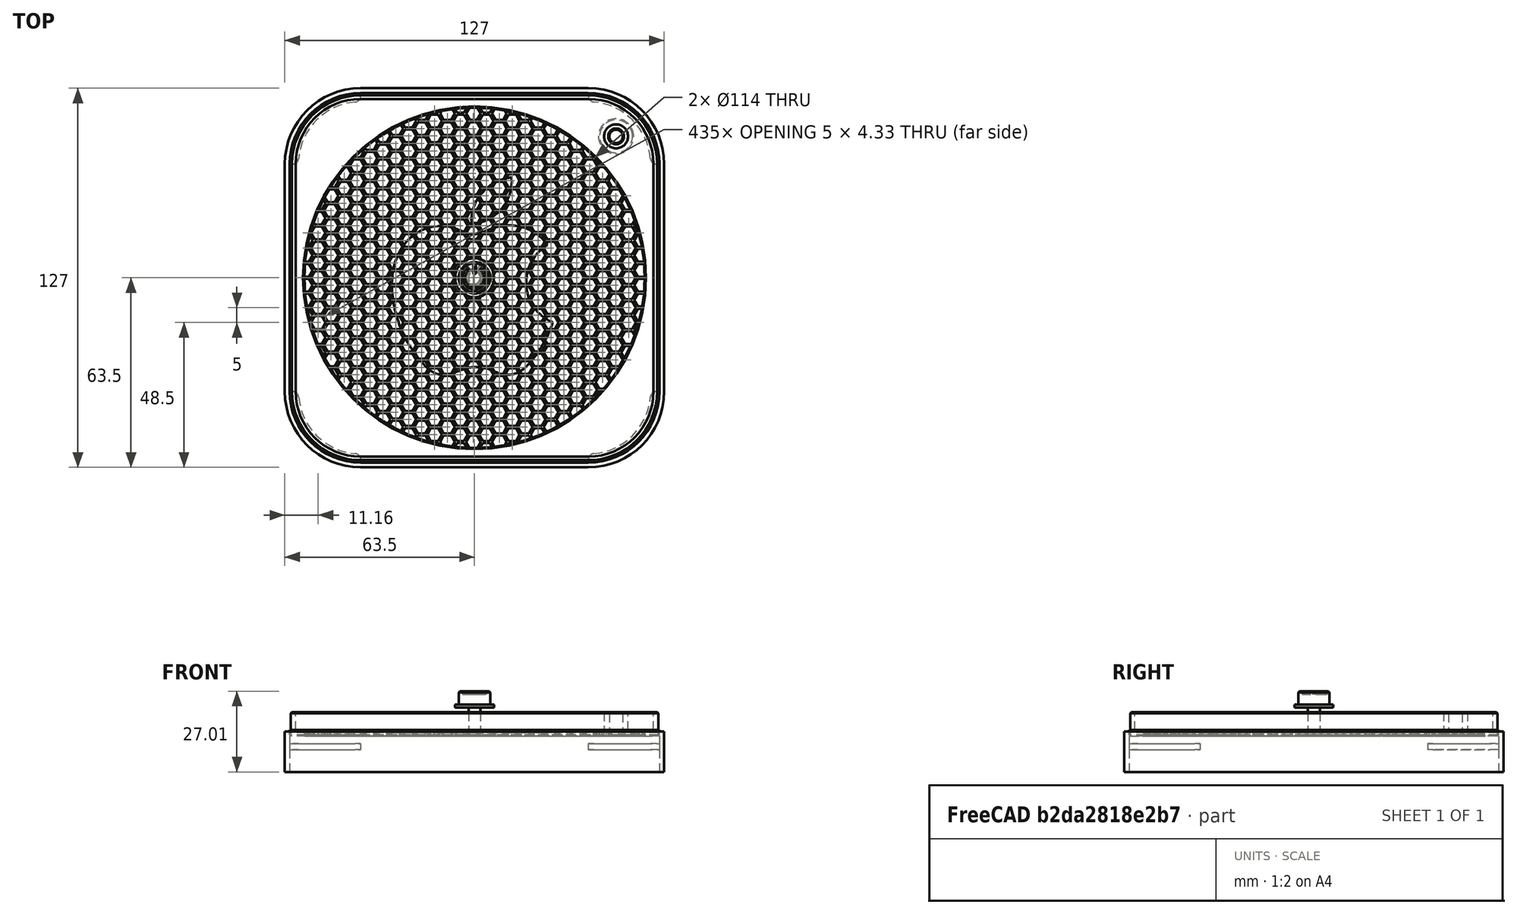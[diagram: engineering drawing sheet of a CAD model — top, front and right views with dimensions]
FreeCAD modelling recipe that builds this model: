
FCSTD DOCUMENT  (FreeCAD 1.0R39104 (Git))
Label: dust shroud for mac mini
License: All rights reserved
LicenseURL: http://en.wikipedia.org/wiki/All_rights_reserved
objects: Sketcher::SketchObject×13, PartDesign::Pad×8, PartDesign::Body×6, PartDesign::SubShapeBinder×4, PartDesign::Chamfer×3, Part::Extrusion×2, Part::Compound×2, App::FeaturePython×1, Part::FeaturePython×1, Part::Cylinder×1, Part::Cut×1, PartDesign::PolarPattern×1, Part::MultiFuse×1, PartDesign::Revolution×1
note: 81 computed .brp shape members not serialized (recipe doc carries the construction recipe); baked Part::Feature solids carry a one-line shape summary decoded from their .brp

FEATURE [App::FeaturePython] dd  # WARN: FeaturePython — macro-defined, semantics opaque (R4)
  BaseFloor = 2
  BaseWallHeight = 8
  BoxRadius = 25.4
  BoxWidth = 127
  ButtonDiameter = 11
  ButtonDistance = 67
  DynamicData = Created with DynamicData (v2.68) workbench. | This is a simple container object built | for holding custom properties.
  FrictionFit = 0
  Fudge = 0.4
  HexSize = 5
  HexSpacing = 5
  HexThickness = 1.6
  MeshThickness = 0.5
  RetainerThickness = 2
  RiserAngle = 0
  RiserHeight = 0
  RiserOuter = 114
  RiserTop = 97
  TopHeight = 12
  TopThickness = 1.6
  Wall = 1.6
  expr: HexThickness = TopThickness
FEATURE [Sketcher::SketchObject] Sketch005  label="master"
  ArcFitTolerance = 1e-06
  FullyConstrained = true
  MakeInternals = false
  MapMode = 5
  expr: Constraints[1] = dd.RiserOuter
  expr: Constraints[41] = dd.Wall
  expr: Constraints[5] = dd.ButtonDistance
  expr: Constraints[6] = dd.ButtonDiameter
  expr: Constraints[79] = dd.Fudge
  expr: Constraints[80] = dd.Wall
  expr: Constraints[81] = dd.RiserTop
  expr: Constraints[83] = dd.BoxRadius
  expr: Constraints[84] = dd.BoxWidth
  sketch-geometry (36):
    g0: Circle CenterX=3.1e-15 CenterY=3.4e-15 CenterZ=0 NormalX=0 NormalY=0 NormalZ=1 AngleXU=0 Radius=57
    g1: Circle CenterX=47.3762 CenterY=47.3762 CenterZ=0 NormalX=0 NormalY=0 NormalZ=1 AngleXU=0 Radius=5.5
    g2: LineSegment [constr] StartX=47.3762 StartY=47.3762 StartZ=0 EndX=3.1e-15 EndY=3.4e-15 EndZ=0
    g3: LineSegment StartX=-63.5 StartY=38.1 StartZ=0 EndX=-63.5 EndY=-38.1 EndZ=0
    g4: LineSegment StartX=-38.1 StartY=-63.5 StartZ=0 EndX=38.1 EndY=-63.5 EndZ=0
    g5: LineSegment StartX=63.5 StartY=-38.1 StartZ=0 EndX=63.5 EndY=38.1 EndZ=0
    g6: LineSegment StartX=38.1 StartY=63.5 StartZ=0 EndX=-38.1 EndY=63.5 EndZ=0
    g7: ArcOfCircle CenterX=-38.1 CenterY=38.1 CenterZ=0 NormalX=0 NormalY=0 NormalZ=1 AngleXU=0 Radius=25.4 StartAngle=1.5708 EndAngle=3.14159
    g8: ArcOfCircle CenterX=-38.1 CenterY=-38.1 CenterZ=0 NormalX=0 NormalY=0 NormalZ=1 AngleXU=0 Radius=25.4 StartAngle=3.14159 EndAngle=4.71239
    g9: ArcOfCircle CenterX=38.1 CenterY=-38.1 CenterZ=0 NormalX=0 NormalY=0 NormalZ=1 AngleXU=0 Radius=25.4 StartAngle=4.71239 EndAngle=6.28319
    g10: ArcOfCircle CenterX=38.1 CenterY=38.1 CenterZ=0 NormalX=0 NormalY=0 NormalZ=1 AngleXU=0 Radius=25.4 StartAngle=0 EndAngle=1.5708
    g11: LineSegment StartX=-61.9 StartY=38.1 StartZ=0 EndX=-61.9 EndY=-38.1 EndZ=0
    g12: LineSegment StartX=-38.1 StartY=-61.9 StartZ=0 EndX=38.1 EndY=-61.9 EndZ=0
    g13: LineSegment StartX=61.9 StartY=-38.1 StartZ=0 EndX=61.9 EndY=38.1 EndZ=0
    g14: LineSegment StartX=38.1 StartY=61.9 StartZ=0 EndX=-38.1 EndY=61.9 EndZ=0
    g15: ArcOfCircle CenterX=-38.1 CenterY=38.1 CenterZ=0 NormalX=0 NormalY=0 NormalZ=1 AngleXU=0 Radius=23.8 StartAngle=1.5708 EndAngle=3.14159
    g16: ArcOfCircle CenterX=-38.1 CenterY=-38.1 CenterZ=0 NormalX=0 NormalY=0 NormalZ=1 AngleXU=0 Radius=23.8 StartAngle=3.14159 EndAngle=4.71239
    g17: ArcOfCircle CenterX=38.1 CenterY=-38.1 CenterZ=0 NormalX=0 NormalY=0 NormalZ=1 AngleXU=0 Radius=23.8 StartAngle=4.71239 EndAngle=6.28319
    g18: ArcOfCircle CenterX=38.1 CenterY=38.1 CenterZ=0 NormalX=0 NormalY=0 NormalZ=1 AngleXU=0 Radius=23.8 StartAngle=-2.6086e-12 EndAngle=1.5708
    g19: Circle CenterX=3.1e-15 CenterY=3.4e-15 CenterZ=0 NormalX=0 NormalY=0 NormalZ=1 AngleXU=0 Radius=48.5
    g20: LineSegment StartX=-61.5 StartY=38.1 StartZ=0 EndX=-61.5 EndY=-38.1 EndZ=0
    g21: LineSegment StartX=-38.1 StartY=-61.5 StartZ=0 EndX=38.1 EndY=-61.5 EndZ=0
    g22: LineSegment StartX=61.5 StartY=-38.1 StartZ=0 EndX=61.5 EndY=38.1 EndZ=0
    g23: LineSegment StartX=38.1 StartY=61.5 StartZ=0 EndX=-38.1 EndY=61.5 EndZ=0
    g24: ArcOfCircle CenterX=-38.1 CenterY=38.1 CenterZ=0 NormalX=0 NormalY=0 NormalZ=1 AngleXU=0 Radius=23.4 StartAngle=1.5708 EndAngle=3.14159
    g25: ArcOfCircle CenterX=-38.1 CenterY=-38.1 CenterZ=0 NormalX=0 NormalY=0 NormalZ=1 AngleXU=0 Radius=23.4 StartAngle=3.14159 EndAngle=4.71239
    g26: ArcOfCircle CenterX=38.1 CenterY=-38.1 CenterZ=0 NormalX=0 NormalY=0 NormalZ=1 AngleXU=0 Radius=23.4 StartAngle=4.71239 EndAngle=6.28319
    g27: ArcOfCircle CenterX=38.1 CenterY=38.1 CenterZ=0 NormalX=0 NormalY=0 NormalZ=1 AngleXU=0 Radius=23.4 StartAngle=-3.471e-12 EndAngle=1.5708
    g28: LineSegment StartX=-59.9 StartY=38.1 StartZ=0 EndX=-59.9 EndY=-38.1 EndZ=0
    g29: LineSegment StartX=-38.1 StartY=-59.9 StartZ=0 EndX=38.1 EndY=-59.9 EndZ=0
    g30: LineSegment StartX=59.9 StartY=-38.1 StartZ=0 EndX=59.9 EndY=38.1 EndZ=0
    g31: LineSegment StartX=38.1 StartY=59.9 StartZ=0 EndX=-38.1 EndY=59.9 EndZ=0
    g32: ArcOfCircle CenterX=-38.1 CenterY=38.1 CenterZ=0 NormalX=0 NormalY=0 NormalZ=1 AngleXU=0 Radius=21.8 StartAngle=1.5708 EndAngle=3.14159
    g33: ArcOfCircle CenterX=-38.1 CenterY=-38.1 CenterZ=0 NormalX=0 NormalY=0 NormalZ=1 AngleXU=0 Radius=21.8 StartAngle=3.14159 EndAngle=4.71239
    g34: ArcOfCircle CenterX=38.1 CenterY=-38.1 CenterZ=0 NormalX=0 NormalY=0 NormalZ=1 AngleXU=0 Radius=21.8 StartAngle=4.71239 EndAngle=6.28319
    g35: ArcOfCircle CenterX=38.1 CenterY=38.1 CenterZ=0 NormalX=0 NormalY=0 NormalZ=1 AngleXU=0 Radius=21.8 StartAngle=-1.30367e-11 EndAngle=1.5708
  constraints (85):
    c: Coincident(g0,g-1)
    c: Diameter(g0) = 114
    c: Coincident(g2,g1)
    c: Coincident(g2,g0)
    c: Angle(g-1,g2) = 0.785398
    c: Distance(g2) = 67
    c: Diameter(g1) = 11
    c: Tangent(g3,g7) = -1.5708
    c: Tangent(g3,g8) = -1.5708
    c: Tangent(g4,g8) = -1.5708
    c: Tangent(g4,g9) = -1.5708
    c: Tangent(g5,g9) = -1.5708
    c: Tangent(g5,g10) = -1.5708
    c: Tangent(g6,g10) = -1.5708
    c: Tangent(g6,g7) = -1.5708
    c: Vertical(g3)
    c: Vertical(g5)
    c: Horizontal(g4)
    c: Horizontal(g6)
    c: Equal(g7,g8)
    c: Equal(g8,g9)
    c: Equal(g9,g10)
    c: Symmetric(g8,g10,g0)
    c: Equal(g6,g3)
    c: Tangent(g11,g15) = -1.5708
    c: Tangent(g11,g16) = -1.5708
    c: Tangent(g12,g16) = -1.5708
    c: Tangent(g12,g17) = -1.5708
    c: Tangent(g13,g17) = -1.5708
    c: Tangent(g13,g18) = -1.5708
    c: Tangent(g14,g18) = -1.5708
    c: Tangent(g14,g15) = -1.5708
    c: Vertical(g11)
    c: Vertical(g13)
    c: Horizontal(g12)
    c: Horizontal(g14)
    c: Equal(g15,g16)
    c: Equal(g16,g17)
    c: Equal(g17,g18)
    c: Symmetric(g16,g18,g0)
    c: Equal(g14,g11)
    c: DistanceY(g14,g6) = 1.6
    c: Coincident(g19,g0)
    c: Tangent(g20,g24) = -1.5708
    c: Tangent(g20,g25) = -1.5708
    c: Tangent(g21,g25) = -1.5708
    c: Tangent(g21,g26) = -1.5708
    c: Tangent(g22,g26) = -1.5708
    c: Tangent(g22,g27) = -1.5708
    c: Tangent(g23,g27) = -1.5708
    c: Tangent(g23,g24) = -1.5708
    c: Vertical(g20)
    c: Vertical(g22)
    c: Horizontal(g21)
    c: Horizontal(g23)
    c: Equal(g24,g25)
    c: Equal(g25,g26)
    c: Equal(g26,g27)
    c: Symmetric(g27,g25,g0)
    c: Equal(g23,g20)
    c: Vertical(g23,g14)
    c: Tangent(g28,g32) = -1.5708
    c: Tangent(g28,g33) = -1.5708
    c: Tangent(g29,g33) = -1.5708
    c: Tangent(g29,g34) = -1.5708
    c: Tangent(g30,g34) = -1.5708
    c: Tangent(g30,g35) = -1.5708
    c: Tangent(g31,g35) = -1.5708
    c: Tangent(g31,g32) = -1.5708
    c: Vertical(g28)
    c: Vertical(g30)
    c: Horizontal(g29)
    c: Horizontal(g31)
    c: Equal(g32,g33)
    c: Equal(g33,g34)
    c: Equal(g34,g35)
    c: Symmetric(g33,g35,g0)
    c: Equal(g30,g31)
    c: Vertical(g31,g23)
    c: DistanceY(g23,g14) = 0.4
    c: DistanceY(g31,g23) = 1.6
    c: Diameter(g19) = 97
    c: Vertical(g14,g6)
    c: Radius(g7) = 25.4
    c: DistanceX(g3,g5) = 127
FEATURE [PartDesign::SubShapeBinder] Binder
  BindCopyOnChange = 0
  BindMode = 0
  ClaimChildren = false
  Context = -> Body003 [Binder.]
  Fuse = false
  MakeFace = true
  OffsetFill = false
  OffsetIntersection = false
  OffsetJoinType = 0
  OffsetOpenResult = false
  PartialLoad = false
  Refine = true
  Relative = true
  Support = -> [Sketch005]
  _Version = 2
FEATURE [Sketcher::SketchObject] Sketch006
  ArcFitTolerance = 1e-06
  AttachmentSupport = -> [XY_Plane003]
  ExternalGeometry = -> [Binder]
  FullyConstrained = true
  MakeInternals = false
  MapMode = 5
  sketch-geometry (12):
    g0: Circle CenterX=0 CenterY=0 CenterZ=0 NormalX=0 NormalY=0 NormalZ=1 AngleXU=0 Radius=57
    g1: Circle CenterX=47.3762 CenterY=47.3762 CenterZ=0 NormalX=0 NormalY=0 NormalZ=1 AngleXU=0 Radius=5.5
    g2: LineSegment StartX=-63.5 StartY=38.1 StartZ=0 EndX=-63.5 EndY=-38.1 EndZ=0
    g3: LineSegment StartX=-38.1 StartY=-63.5 StartZ=0 EndX=38.1 EndY=-63.5 EndZ=0
    g4: LineSegment StartX=63.5 StartY=-38.1 StartZ=0 EndX=63.5 EndY=38.1 EndZ=0
    g5: LineSegment StartX=38.1 StartY=63.5 StartZ=0 EndX=-38.1 EndY=63.5 EndZ=0
    g6: ArcOfCircle CenterX=-38.1 CenterY=38.1 CenterZ=0 NormalX=0 NormalY=0 NormalZ=1 AngleXU=0 Radius=25.4 StartAngle=1.5708 EndAngle=3.14159
    g7: ArcOfCircle CenterX=-38.1 CenterY=-38.1 CenterZ=0 NormalX=0 NormalY=0 NormalZ=1 AngleXU=0 Radius=25.4 StartAngle=3.14159 EndAngle=4.71239
    g8: ArcOfCircle CenterX=38.1 CenterY=-38.1 CenterZ=0 NormalX=0 NormalY=0 NormalZ=1 AngleXU=0 Radius=25.4 StartAngle=4.71239 EndAngle=6.28319
    g9: ArcOfCircle CenterX=38.1 CenterY=38.1 CenterZ=0 NormalX=0 NormalY=0 NormalZ=1 AngleXU=0 Radius=25.4 StartAngle=0 EndAngle=1.5708
    g10: GeomPoint [constr] X=-63.5 Y=63.5 Z=0
    g11: GeomPoint [constr] X=63.5 Y=-63.5 Z=0
  constraints (26):
    c: Coincident(g0,g-1)
    c: Coincident(g1,g-5)
    c: Equal(g1,g-5)
    c: Equal(g0,g-4)
    c: Tangent(g2,g6) = -1.5708
    c: Tangent(g2,g7) = -1.5708
    c: Tangent(g3,g7) = -1.5708
    c: Tangent(g3,g8) = -1.5708
    c: Tangent(g4,g8) = -1.5708
    c: Tangent(g4,g9) = -1.5708
    c: Tangent(g5,g9) = -1.5708
    c: Tangent(g5,g6) = -1.5708
    c: Vertical(g2)
    c: Vertical(g4)
    c: Horizontal(g3)
    c: Horizontal(g5)
    c: Equal(g6,g7)
    c: Equal(g7,g8)
    c: Equal(g8,g9)
    c: PointOnObject(g10,g2)
    c: PointOnObject(g10,g5)
    c: PointOnObject(g11,g3)
    c: PointOnObject(g11,g4)
    c: Equal(g5,g2)
    c: Symmetric(g6,g8,g0)
    c: Coincident(g5,g-3)
FEATURE [PartDesign::Pad] Pad004
  Direction = (0,0,1)
  Length = 1.6
  Length2 = 10
  Profile = -> Sketch006
  ReferenceAxis = -> Sketch006 [N_Axis]
  Refine = true
  Suppressed = false
  Type = 0
  expr: Length = dd.TopThickness
FEATURE [Sketcher::SketchObject] Sketch007
  ArcFitTolerance = 1e-06
  AttachmentSupport = -> [XY_Plane003]
  ExternalGeometry = -> [Binder]
  FullyConstrained = true
  MakeInternals = false
  MapMode = 5
  sketch-geometry (20):
    g0: LineSegment StartX=-61.9 StartY=38.1 StartZ=0 EndX=-61.9 EndY=-38.1 EndZ=0
    g1: LineSegment StartX=-38.1 StartY=-61.9 StartZ=0 EndX=38.1 EndY=-61.9 EndZ=0
    g2: LineSegment StartX=61.9 StartY=-38.1 StartZ=0 EndX=61.9 EndY=38.1 EndZ=0
    g3: LineSegment StartX=38.1 StartY=61.9 StartZ=0 EndX=-38.1 EndY=61.9 EndZ=0
    g4: ArcOfCircle CenterX=-38.1 CenterY=38.1 CenterZ=0 NormalX=0 NormalY=0 NormalZ=1 AngleXU=0 Radius=23.8 StartAngle=1.5708 EndAngle=3.14159
    g5: ArcOfCircle CenterX=-38.1 CenterY=-38.1 CenterZ=0 NormalX=0 NormalY=0 NormalZ=1 AngleXU=0 Radius=23.8 StartAngle=3.14159 EndAngle=4.71239
    g6: ArcOfCircle CenterX=38.1 CenterY=-38.1 CenterZ=0 NormalX=0 NormalY=0 NormalZ=1 AngleXU=0 Radius=23.8 StartAngle=4.71239 EndAngle=6.28319
    g7: ArcOfCircle CenterX=38.1 CenterY=38.1 CenterZ=0 NormalX=0 NormalY=0 NormalZ=1 AngleXU=0 Radius=23.8 StartAngle=0 EndAngle=1.5708
    g8: GeomPoint [constr] X=-61.9 Y=61.9 Z=0
    g9: GeomPoint [constr] X=61.9 Y=-61.9 Z=0
    g10: LineSegment StartX=-63.5 StartY=38.1 StartZ=0 EndX=-63.5 EndY=-38.1 EndZ=0
    g11: LineSegment StartX=-38.1 StartY=-63.5 StartZ=0 EndX=38.1 EndY=-63.5 EndZ=0
    g12: LineSegment StartX=63.5 StartY=-38.1 StartZ=0 EndX=63.5 EndY=38.1 EndZ=0
    g13: LineSegment StartX=38.1 StartY=63.5 StartZ=0 EndX=-38.1 EndY=63.5 EndZ=0
    g14: ArcOfCircle CenterX=-38.1 CenterY=38.1 CenterZ=0 NormalX=0 NormalY=0 NormalZ=1 AngleXU=0 Radius=25.4 StartAngle=1.5708 EndAngle=3.14159
    g15: ArcOfCircle CenterX=-38.1 CenterY=-38.1 CenterZ=0 NormalX=0 NormalY=0 NormalZ=1 AngleXU=0 Radius=25.4 StartAngle=3.14159 EndAngle=4.71239
    g16: ArcOfCircle CenterX=38.1 CenterY=-38.1 CenterZ=0 NormalX=0 NormalY=0 NormalZ=1 AngleXU=0 Radius=25.4 StartAngle=4.71239 EndAngle=6.28319
    g17: ArcOfCircle CenterX=38.1 CenterY=38.1 CenterZ=0 NormalX=0 NormalY=0 NormalZ=1 AngleXU=0 Radius=25.4 StartAngle=0 EndAngle=1.5708
    g18: GeomPoint [constr] X=-63.5 Y=63.5 Z=0
    g19: GeomPoint [constr] X=63.5 Y=-63.5 Z=0
  constraints (44):
    c: Tangent(g0,g4) = -1.5708
    c: Tangent(g0,g5) = -1.5708
    c: Tangent(g1,g5) = -1.5708
    c: Tangent(g1,g6) = -1.5708
    c: Tangent(g2,g6) = -1.5708
    c: Tangent(g2,g7) = -1.5708
    c: Tangent(g3,g7) = -1.5708
    c: Tangent(g3,g4) = -1.5708
    c: Vertical(g0)
    c: Vertical(g2)
    c: Horizontal(g1)
    c: Horizontal(g3)
    c: Equal(g4,g5)
    c: Equal(g5,g6)
    c: Equal(g6,g7)
    c: PointOnObject(g8,g0)
    c: PointOnObject(g8,g3)
    c: PointOnObject(g9,g1)
    c: PointOnObject(g9,g2)
    c: Tangent(g10,g14) = -1.5708
    c: Tangent(g10,g15) = -1.5708
    c: Tangent(g11,g15) = -1.5708
    c: Tangent(g11,g16) = -1.5708
    c: Tangent(g12,g16) = -1.5708
    c: Tangent(g12,g17) = -1.5708
    c: Tangent(g13,g17) = -1.5708
    c: Tangent(g13,g14) = -1.5708
    c: Vertical(g10)
    c: Vertical(g12)
    c: Horizontal(g11)
    c: Horizontal(g13)
    c: Equal(g14,g15)
    c: Equal(g15,g16)
    c: Equal(g16,g17)
    c: PointOnObject(g18,g10)
    c: PointOnObject(g18,g13)
    c: PointOnObject(g19,g11)
    c: PointOnObject(g19,g12)
    c: Equal(g10,g13)
    c: Symmetric(g14,g16,g-1)
    c: Symmetric(g9,g8,g-1)
    c: Coincident(g13,g-3)
    c: Coincident(g3,g-4)
    c: Equal(g0,g3)
FEATURE [PartDesign::Pad] Pad005
  BaseFeature = -> Pad004
  Direction = (0,0,1)
  Length = 12
  Length2 = 10
  Profile = -> Sketch007
  ReferenceAxis = -> Sketch007 [N_Axis]
  Refine = true
  Reversed = true
  Suppressed = false
  Type = 0
  expr: Length = dd.TopHeight
FEATURE [PartDesign::SubShapeBinder] Binder001
  BindCopyOnChange = 0
  BindMode = 0
  ClaimChildren = false
  Context = -> Body [Binder001.]
  Fuse = false
  MakeFace = true
  OffsetFill = false
  OffsetIntersection = false
  OffsetJoinType = 0
  OffsetOpenResult = false
  PartialLoad = false
  Refine = true
  Relative = true
  Support = -> [Sketch005]
  _Version = 2
FEATURE [Sketcher::SketchObject] Sketch
  ArcFitTolerance = 1e-06
  AttachmentSupport = -> [XY_Plane]
  ExternalGeometry = -> [Binder001]
  FullyConstrained = true
  MakeInternals = false
  MapMode = 5
  expr: Constraints[25] = dd.FrictionFit
  sketch-geometry (12):
    g0: Circle CenterX=47.3762 CenterY=47.3762 CenterZ=0 NormalX=0 NormalY=0 NormalZ=1 AngleXU=0 Radius=2.25
    g1: Circle CenterX=0 CenterY=0 CenterZ=0 NormalX=0 NormalY=0 NormalZ=1 AngleXU=0 Radius=57
    g2: LineSegment StartX=-61.9 StartY=38.1 StartZ=0 EndX=-61.9 EndY=-38.1 EndZ=0
    g3: LineSegment StartX=-38.1 StartY=-61.9 StartZ=0 EndX=38.1 EndY=-61.9 EndZ=0
    g4: LineSegment StartX=61.9 StartY=-38.1 StartZ=0 EndX=61.9 EndY=38.1 EndZ=0
    g5: LineSegment StartX=38.1 StartY=61.9 StartZ=0 EndX=-38.1 EndY=61.9 EndZ=0
    g6: ArcOfCircle CenterX=-38.1 CenterY=38.1 CenterZ=0 NormalX=0 NormalY=0 NormalZ=1 AngleXU=0 Radius=23.8 StartAngle=1.5708 EndAngle=3.14159
    g7: ArcOfCircle CenterX=-38.1 CenterY=-38.1 CenterZ=0 NormalX=0 NormalY=0 NormalZ=1 AngleXU=0 Radius=23.8 StartAngle=3.14159 EndAngle=4.71239
    g8: ArcOfCircle CenterX=38.1 CenterY=-38.1 CenterZ=0 NormalX=0 NormalY=0 NormalZ=1 AngleXU=0 Radius=23.8 StartAngle=4.71239 EndAngle=6.28319
    g9: ArcOfCircle CenterX=38.1 CenterY=38.1 CenterZ=0 NormalX=0 NormalY=0 NormalZ=1 AngleXU=0 Radius=23.8 StartAngle=0 EndAngle=1.5708
    g10: GeomPoint [constr] X=-61.9 Y=61.9 Z=0
    g11: GeomPoint [constr] X=61.9 Y=-61.9 Z=0
  constraints (27):
    c: Coincident(g0,g-3)
    c: Coincident(g1,g-1)
    c: Equal(g1,g-4)
    c: Tangent(g2,g6) = -1.5708
    c: Tangent(g2,g7) = -1.5708
    c: Tangent(g3,g7) = -1.5708
    c: Tangent(g3,g8) = -1.5708
    c: Tangent(g4,g8) = -1.5708
    c: Tangent(g4,g9) = -1.5708
    c: Tangent(g5,g9) = -1.5708
    c: Tangent(g5,g6) = -1.5708
    c: Vertical(g2)
    c: Vertical(g4)
    c: Horizontal(g3)
    c: Horizontal(g5)
    c: Equal(g6,g7)
    c: Equal(g7,g8)
    c: Equal(g8,g9)
    c: PointOnObject(g10,g2)
    c: PointOnObject(g10,g5)
    c: PointOnObject(g11,g3)
    c: PointOnObject(g11,g4)
    c: Symmetric(g7,g9,g1)
    c: Equal(g5,g2)
    c: Vertical(g5,g-5)
    c: DistanceY(g5,g-5) = 0
    c: Diameter(g0) = 4.5
FEATURE [PartDesign::Pad] Pad
  Direction = (0,0,1)
  Length = 2
  Length2 = 10
  Profile = -> Sketch
  ReferenceAxis = -> Sketch [N_Axis]
  Refine = true
  Suppressed = false
  Type = 0
  expr: Length = dd.BaseFloor
FEATURE [Sketcher::SketchObject] Sketch008
  ArcFitTolerance = 1e-06
  AttachmentSupport = -> [XY_Plane]
  ExternalGeometry = -> [Binder001]
  FullyConstrained = true
  MakeInternals = false
  MapMode = 5
  sketch-geometry (20):
    g0: LineSegment StartX=-59.9 StartY=38.1 StartZ=0 EndX=-59.9 EndY=-38.1 EndZ=0
    g1: LineSegment StartX=-38.1 StartY=-59.9 StartZ=0 EndX=38.1 EndY=-59.9 EndZ=0
    g2: LineSegment StartX=59.9 StartY=-38.1 StartZ=0 EndX=59.9 EndY=38.1 EndZ=0
    g3: LineSegment StartX=38.1 StartY=59.9 StartZ=0 EndX=-38.1 EndY=59.9 EndZ=0
    g4: ArcOfCircle CenterX=-38.1 CenterY=38.1 CenterZ=0 NormalX=0 NormalY=0 NormalZ=1 AngleXU=0 Radius=21.8 StartAngle=1.5708 EndAngle=3.14159
    g5: ArcOfCircle CenterX=-38.1 CenterY=-38.1 CenterZ=0 NormalX=0 NormalY=0 NormalZ=1 AngleXU=0 Radius=21.8 StartAngle=3.14159 EndAngle=4.71239
    g6: ArcOfCircle CenterX=38.1 CenterY=-38.1 CenterZ=0 NormalX=0 NormalY=0 NormalZ=1 AngleXU=0 Radius=21.8 StartAngle=4.71239 EndAngle=6.28319
    g7: ArcOfCircle CenterX=38.1 CenterY=38.1 CenterZ=0 NormalX=0 NormalY=0 NormalZ=1 AngleXU=0 Radius=21.8 StartAngle=1e-16 EndAngle=1.5708
    g8: GeomPoint [constr] X=-59.9 Y=59.9 Z=0
    g9: GeomPoint [constr] X=59.9 Y=-59.9 Z=0
    g10: LineSegment StartX=-61.5 StartY=38.1 StartZ=0 EndX=-61.5 EndY=-38.1 EndZ=0
    g11: LineSegment StartX=-38.1 StartY=-61.5 StartZ=0 EndX=38.1 EndY=-61.5 EndZ=0
    g12: LineSegment StartX=61.5 StartY=-38.1 StartZ=0 EndX=61.5 EndY=38.1 EndZ=0
    g13: LineSegment StartX=38.1 StartY=61.5 StartZ=0 EndX=-38.1 EndY=61.5 EndZ=0
    g14: ArcOfCircle CenterX=-38.1 CenterY=38.1 CenterZ=0 NormalX=0 NormalY=0 NormalZ=1 AngleXU=0 Radius=23.4 StartAngle=1.5708 EndAngle=3.14159
    g15: ArcOfCircle CenterX=-38.1 CenterY=-38.1 CenterZ=0 NormalX=0 NormalY=0 NormalZ=1 AngleXU=0 Radius=23.4 StartAngle=3.14159 EndAngle=4.71239
    g16: ArcOfCircle CenterX=38.1 CenterY=-38.1 CenterZ=0 NormalX=0 NormalY=0 NormalZ=1 AngleXU=0 Radius=23.4 StartAngle=4.71239 EndAngle=6.28319
    g17: ArcOfCircle CenterX=38.1 CenterY=38.1 CenterZ=0 NormalX=0 NormalY=0 NormalZ=1 AngleXU=0 Radius=23.4 StartAngle=1e-16 EndAngle=1.5708
    g18: GeomPoint [constr] X=-61.5 Y=61.5 Z=0
    g19: GeomPoint [constr] X=61.5 Y=-61.5 Z=0
  constraints (44):
    c: Tangent(g0,g4) = -1.5708
    c: Tangent(g0,g5) = -1.5708
    c: Tangent(g1,g5) = -1.5708
    c: Tangent(g1,g6) = -1.5708
    c: Tangent(g2,g6) = -1.5708
    c: Tangent(g2,g7) = -1.5708
    c: Tangent(g3,g7) = -1.5708
    c: Tangent(g3,g4) = -1.5708
    c: Vertical(g0)
    c: Vertical(g2)
    c: Horizontal(g1)
    c: Horizontal(g3)
    c: Equal(g4,g5)
    c: Equal(g5,g6)
    c: Equal(g6,g7)
    c: PointOnObject(g8,g0)
    c: PointOnObject(g8,g3)
    c: PointOnObject(g9,g1)
    c: PointOnObject(g9,g2)
    c: Tangent(g10,g14) = -1.5708
    c: Tangent(g10,g15) = -1.5708
    c: Tangent(g11,g15) = -1.5708
    c: Tangent(g11,g16) = -1.5708
    c: Tangent(g12,g16) = -1.5708
    c: Tangent(g12,g17) = -1.5708
    c: Tangent(g13,g17) = -1.5708
    c: Tangent(g13,g14) = -1.5708
    c: Vertical(g10)
    c: Vertical(g12)
    c: Horizontal(g11)
    c: Horizontal(g13)
    c: Equal(g14,g15)
    c: Equal(g15,g16)
    c: Equal(g16,g17)
    c: PointOnObject(g18,g10)
    c: PointOnObject(g18,g13)
    c: PointOnObject(g19,g11)
    c: PointOnObject(g19,g12)
    c: Equal(g10,g13)
    c: Equal(g3,g0)
    c: Symmetric(g4,g6,g-1)
    c: Symmetric(g14,g16,g-1)
    c: Coincident(g13,g-4)
    c: Coincident(g3,g-3)
FEATURE [PartDesign::Pad] Pad006
  BaseFeature = -> Pad
  Direction = (0,0,1)
  Length = 8
  Length2 = 10
  Profile = -> Sketch008
  ReferenceAxis = -> Sketch008 [N_Axis]
  Refine = true
  Suppressed = false
  Type = 0
  expr: Length = dd.BaseWallHeight
FEATURE [Sketcher::SketchObject] Sketch011
  ArcFitTolerance = 1e-06
  FullyConstrained = true
  MakeInternals = false
  expr: Constraints[39] = dd.HexSpacing
  expr: Constraints[40] = dd.HexSize
  sketch-geometry (15):
    g0: LineSegment StartX=1.25 StartY=-2.16506 StartZ=0 EndX=2.5 EndY=8e-16 EndZ=0
    g1: LineSegment StartX=2.5 StartY=8e-16 StartZ=0 EndX=1.25 EndY=2.16506 EndZ=0
    g2: LineSegment StartX=1.25 StartY=2.16506 StartZ=0 EndX=-1.25 EndY=2.16506 EndZ=0
    g3: LineSegment StartX=-1.25 StartY=2.16506 StartZ=0 EndX=-2.5 EndY=2.84e-14 EndZ=0
    g4: LineSegment StartX=-2.5 StartY=2.84e-14 StartZ=0 EndX=-1.25 EndY=-2.16506 EndZ=0
    g5: LineSegment StartX=-1.25 StartY=-2.16506 StartZ=0 EndX=1.25 EndY=-2.16506 EndZ=0
    g6: Circle [constr] CenterX=-2e-16 CenterY=0 CenterZ=0 NormalX=0 NormalY=0 NormalZ=1 AngleXU=0 Radius=2.5
    g7: LineSegment StartX=5.58013 StartY=-4.66506 StartZ=0 EndX=6.83013 EndY=-2.5 EndZ=0
    g8: LineSegment StartX=6.83013 StartY=-2.5 StartZ=0 EndX=5.58013 EndY=-0.334936 EndZ=0
    g9: LineSegment StartX=5.58013 StartY=-0.334936 StartZ=0 EndX=3.08013 EndY=-0.334936 EndZ=0
    g10: LineSegment StartX=3.08013 StartY=-0.334936 StartZ=0 EndX=1.83013 EndY=-2.5 EndZ=0
    g11: LineSegment StartX=1.83013 StartY=-2.5 StartZ=0 EndX=3.08013 EndY=-4.66506 EndZ=0
    g12: LineSegment StartX=3.08013 StartY=-4.66506 StartZ=0 EndX=5.58013 EndY=-4.66506 EndZ=0
    g13: Circle [constr] CenterX=4.33013 CenterY=-2.5 CenterZ=0 NormalX=0 NormalY=0 NormalZ=1 AngleXU=0 Radius=2.5
    g14: LineSegment [constr] StartX=4.33013 StartY=-2.5 StartZ=0 EndX=-2e-16 EndY=0 EndZ=0
  constraints (35):
    c: Coincident(g0,g1)
    c: Coincident(g1,g2)
    c: Coincident(g2,g3)
    c: Coincident(g3,g4)
    c: Coincident(g4,g5)
    c: Coincident(g5,g0)
    c: Equal(g0, g1-g5) x5
    c: PointOnObject(g0,g6)
    c: PointOnObject(g1,g6)
    c: PointOnObject(g2,g6)
    c: PointOnObject(g3,g6)
    c: PointOnObject(g4,g6)
    c: PointOnObject(g5,g6)
    c: Coincident(g7,g8)
    c: Coincident(g8,g9)
    c: Coincident(g9,g10)
    c: Coincident(g10,g11)
    c: Coincident(g11,g12)
    c: Coincident(g12,g7)
    c: Equal(g7, g8-g12) x5
    c: PointOnObject(g7,g13)
    c: PointOnObject(g8,g13)
    c: PointOnObject(g9,g13)
    c: PointOnObject(g10,g13)
    c: PointOnObject(g11,g13)
    c: PointOnObject(g12,g13)
    c: Horizontal(g12)
    c: Horizontal(g5)
    c: Equal(g6,g13)
    c: Coincident(g14,g13)
    c: Coincident(g14,g6)
    c: Perpendicular(g10,g14) = 5
    c: Distance(g14) = 5
    c: Diameter(g13) = 5
    c: Coincident(g6,g-1)
FEATURE [Part::FeaturePython] Array  # Draft array (typed FeaturePython)
  AlwaysSyncPlacement = false
  Angle = 360
  ArrayType = 0
  Axis = (0,0,1)
  Base = -> Sketch011
  Center = (0,0,0)
  Count = 350
  ExpandArray = false
  Fuse = false
  IntervalAxis = (0,0,0)
  IntervalX = (8.66025,0,0)
  IntervalY = (0,5,0)
  IntervalZ = (0,0,100)
  NumberCircles = 3
  NumberPolar = 5
  NumberX = 14
  NumberY = 25
  NumberZ = 1
  Placement = pos=(-61,-60,0) rot=(0,0,1;0rad)
  PlacementList = 350 placements: [(0,0,0),(0,5,0),(0,10,0),(0,15,0),(0,20,0),(0,25,0),(0,30,0),(0,35,0),(0,40,0),(0,45,0),(0,50,0),(0,55,0),(0,60,0),(0,65,0),(0,70,0),(0,75,0),(0,80,0),(0,85,0),(0,90,0),(0,95,0),(0,100,0),(0,105,0),(0,110,0),(0,115,0),(0,120,0),(8.66025,0,0),(8.66025,5,0),(8.66025,10,0),(8.66025,15,0),(8.66025,20,0),(8.66025,25,0),(8.66025,30,0),(8.66025,35,0),(8.66025,40,0),(8.66025,45,0),(8.66025,50,0),+314 more]
  RadialDistance = 50
  Symmetry = 1
  TangentialDistance = 25
  expr: .IntervalX.x = cos(30) * dd.HexSpacing * 2
  expr: .IntervalY.y = dd.HexSpacing
FEATURE [Part::Cylinder] Cylinder
  Angle = 360
  AttacherType = Attacher::AttachEngine3D
  FirstAngle = 0
  Height = 1.6
  Radius = 58
  SecondAngle = 0
  expr: Height = dd.HexThickness
  expr: Radius = (dd.RiserOuter + 2) / 2
FEATURE [Part::Extrusion] Extrude
  Base = -> Array
  Dir = (0,0,1)
  DirMode = 2
  FaceMakerClass = Part::FaceMakerBullseye
  FaceMakerMode = 3
  LengthFwd = 10
  LengthRev = 0
  Placement = pos=(0,0,-2) rot=(0,0,1;0rad)
  Solid = true
  Symmetric = false
FEATURE [Part::Cut] Cut  label="hex grid"
  Base = -> Cylinder
  Refine = true
  Tool = -> Extrude
  expr: .Placement.Base.z = dd.TopThickness - dd.HexThickness
FEATURE [Sketcher::SketchObject] Sketch012
  ArcFitTolerance = 1e-06
  AttachmentOffset = pos=(0,0,2.5) rot=(0,0,1;0rad)
  AttachmentSupport = -> [Pad005]
  ExternalGeometry = -> [Pad005]
  FullyConstrained = true
  MakeInternals = false
  MapMode = 5
  Placement = pos=(0,0,-2.5) rot=(1,0,0;3.14159rad)
  expr: .AttachmentOffset.Base.z = dd.RetainerThickness + 0.5
  sketch-geometry (6):
    g0: ArcOfCircle CenterX=-38.1 CenterY=38.1 CenterZ=0 NormalX=0 NormalY=0 NormalZ=1 AngleXU=0 Radius=20.8799 StartAngle=1.65832 EndAngle=3.05407
    g1: ArcOfCircle CenterX=-38.1 CenterY=38.1 CenterZ=0 NormalX=0 NormalY=0 NormalZ=1 AngleXU=0 Radius=23.8 StartAngle=1.5708 EndAngle=3.14159
    g2: LineSegment StartX=-38.1 StartY=61.9 StartZ=0 EndX=-38.1 EndY=60.8923 EndZ=0
    g3: LineSegment StartX=-60.8923 StartY=38.1 StartZ=0 EndX=-61.9 EndY=38.1 EndZ=0
    g4: ArcOfCircle CenterX=-40.1 CenterY=60.8923 CenterZ=0 NormalX=0 NormalY=0 NormalZ=1 AngleXU=0 Radius=2 StartAngle=4.79991 EndAngle=6.28319
    g5: ArcOfCircle CenterX=-60.8923 CenterY=40.1 CenterZ=0 NormalX=0 NormalY=0 NormalZ=1 AngleXU=0 Radius=2 StartAngle=4.71239 EndAngle=6.19566
  constraints (15):
    c: Coincident(g0,g-3)
    c: Coincident(g1,g0)
    c: Coincident(g1,g-3)
    c: Coincident(g2,g1)
    c: Coincident(g3,g1)
    c: Tangent(g2,g4) = 1.5708
    c: Tangent(g0,g4) = 1.5708
    c: Tangent(g0,g5) = 1.5708
    c: Tangent(g3,g5) = 1.5708
    c: Equal(g5,g4)
    c: Radius(g5) = 2
    c: Vertical(g2)
    c: Vertical(g2,g-3)
    c: Horizontal(g3,g1)
    c: DistanceY(g0,g1) = 3
FEATURE [PartDesign::Pad] Pad007
  BaseFeature = -> Pad005
  Direction = (0,0,-1)
  Length = 2
  Length2 = 10
  Profile = -> Sketch012
  ReferenceAxis = -> Sketch012 [N_Axis]
  Refine = true
  Suppressed = false
  Type = 0
  expr: Length = dd.RetainerThickness
FEATURE [PartDesign::PolarPattern] PolarPattern
  Angle = 360
  Axis = -> Sketch012 [N_Axis]
  BaseFeature = -> Pad007
  Mode = 0
  Occurrences = 4
  Offset = 120
  Originals = -> [Pad007]
  Refine = true
  Suppressed = false
  TransformMode = 0
FEATURE [PartDesign::Body] Body003  label="Top"
  AllowCompound = true
  Group = -> [Binder,Sketch006,Pad004,Sketch007,Pad005,Sketch012,Pad007,PolarPattern]
  Origin = -> Origin003
  Tip = -> PolarPattern
FEATURE [Part::MultiFuse] Fusion  label="Top without logo"
  Refine = true
  Shapes = -> [Cut,Body003]
FEATURE [PartDesign::SubShapeBinder] Binder002
  BindCopyOnChange = 0
  BindMode = 0
  ClaimChildren = false
  Context = -> Body004 [Binder002.]
  Fuse = false
  MakeFace = true
  OffsetFill = false
  OffsetIntersection = false
  OffsetJoinType = 0
  OffsetOpenResult = false
  PartialLoad = false
  Refine = true
  Relative = true
  Support = -> [Sketch005]
  _Version = 2
FEATURE [Sketcher::SketchObject] Sketch013
  ArcFitTolerance = 1e-06
  AttachmentSupport = -> [XY_Plane004]
  ExternalGeometry = -> [Binder002]
  FullyConstrained = true
  MakeInternals = false
  MapMode = 5
  sketch-geometry (12):
    g0: LineSegment StartX=-61.5 StartY=38.1 StartZ=0 EndX=-61.5 EndY=-38.1 EndZ=0
    g1: LineSegment StartX=-38.1 StartY=-61.5 StartZ=0 EndX=38.1 EndY=-61.5 EndZ=0
    g2: LineSegment StartX=61.5 StartY=-38.1 StartZ=0 EndX=61.5 EndY=38.1 EndZ=0
    g3: LineSegment StartX=38.1 StartY=61.5 StartZ=0 EndX=-38.1 EndY=61.5 EndZ=0
    g4: ArcOfCircle CenterX=-38.1 CenterY=38.1 CenterZ=0 NormalX=0 NormalY=0 NormalZ=1 AngleXU=0 Radius=23.4 StartAngle=1.5708 EndAngle=3.14159
    g5: ArcOfCircle CenterX=-38.1 CenterY=-38.1 CenterZ=0 NormalX=0 NormalY=0 NormalZ=1 AngleXU=0 Radius=23.4 StartAngle=3.14159 EndAngle=4.71239
    g6: ArcOfCircle CenterX=38.1 CenterY=-38.1 CenterZ=0 NormalX=0 NormalY=0 NormalZ=1 AngleXU=0 Radius=23.4 StartAngle=4.71239 EndAngle=6.28319
    g7: ArcOfCircle CenterX=38.1 CenterY=38.1 CenterZ=0 NormalX=0 NormalY=0 NormalZ=1 AngleXU=0 Radius=23.4 StartAngle=0 EndAngle=1.5708
    g8: GeomPoint [constr] X=-61.5 Y=61.5 Z=0
    g9: GeomPoint [constr] X=61.5 Y=-61.5 Z=0
    g10: Circle CenterX=0 CenterY=0 CenterZ=0 NormalX=0 NormalY=0 NormalZ=1 AngleXU=0 Radius=57
    g11: Circle CenterX=47.3762 CenterY=47.3762 CenterZ=0 NormalX=0 NormalY=0 NormalZ=1 AngleXU=0 Radius=5.5
  constraints (26):
    c: Tangent(g0,g4) = -1.5708
    c: Tangent(g0,g5) = -1.5708
    c: Tangent(g1,g5) = -1.5708
    c: Tangent(g1,g6) = -1.5708
    c: Tangent(g2,g6) = -1.5708
    c: Tangent(g2,g7) = -1.5708
    c: Tangent(g3,g7) = -1.5708
    c: Tangent(g3,g4) = -1.5708
    c: Vertical(g0)
    c: Vertical(g2)
    c: Horizontal(g1)
    c: Horizontal(g3)
    c: Equal(g4,g5)
    c: Equal(g5,g6)
    c: Equal(g6,g7)
    c: PointOnObject(g8,g0)
    c: PointOnObject(g8,g3)
    c: PointOnObject(g9,g1)
    c: PointOnObject(g9,g2)
    c: Equal(g3,g0)
    c: Symmetric(g4,g6,g-1)
    c: Coincident(g10,g-1)
    c: Coincident(g11,g-4)
    c: Equal(g11,g-4)
    c: Equal(g10,g-3)
    c: Coincident(g3,g-5)
FEATURE [PartDesign::Pad] Pad008
  Direction = (0,0,1)
  Length = 1.5
  Length2 = 10
  Profile = -> Sketch013
  ReferenceAxis = -> Sketch013 [N_Axis]
  Refine = true
  Suppressed = false
  Type = 0
  expr: Length = dd.RetainerThickness - dd.MeshThickness
FEATURE [PartDesign::Chamfer] Chamfer001
  Angle = 45
  Base = -> Pad008 [Face12,Face11]
  BaseFeature = -> Pad008
  ChamferType = 0
  FlipDirection = false
  Refine = true
  Size = 0.4
  Size2 = 1
  SupportTransform = false
  Suppressed = false
  UseAllEdges = false
FEATURE [PartDesign::Body] Body004  label="Retainer panel"
  AllowCompound = false
  Group = -> [Binder002,Sketch013,Pad008,Chamfer001]
  Origin = -> Origin004
  Tip = -> Chamfer001
FEATURE [Sketcher::SketchObject] Sketch014
  ArcFitTolerance = 1e-06
  AttachmentSupport = -> [Pad006]
  ExternalGeometry = -> [Pad006]
  FullyConstrained = true
  MakeInternals = false
  MapMode = 5
  Placement = pos=(0,0,2) rot=(0,0,1;0rad)
  sketch-geometry (2):
    g0: Circle CenterX=47.3762 CenterY=47.3762 CenterZ=0 NormalX=0 NormalY=0 NormalZ=1 AngleXU=0 Radius=2.25
    g1: Circle CenterX=47.3762 CenterY=47.3762 CenterZ=0 NormalX=0 NormalY=0 NormalZ=1 AngleXU=0 Radius=4
  constraints (4):
    c: Coincident(g0,g-3)
    c: Equal(g0,g-3)
    c: Coincident(g1,g0)
    c: Diameter(g1) = 8
FEATURE [PartDesign::Pad] Pad009
  BaseFeature = -> Pad006
  Direction = (0,0,1)
  Length = 10
  Length2 = 10
  Profile = -> Sketch014
  ReferenceAxis = -> Sketch014 [N_Axis]
  Refine = true
  Suppressed = false
  Type = 3
  UpToFace = -> Pad006 [Face18]
FEATURE [PartDesign::Chamfer] Chamfer
  Angle = 45
  Base = -> Pad009 [Edge36,Edge80,Edge49,Face4]
  BaseFeature = -> Pad009
  ChamferType = 0
  FlipDirection = false
  Refine = true
  Size = 0.4
  Size2 = 1
  SupportTransform = false
  Suppressed = false
  UseAllEdges = false
FEATURE [PartDesign::Body] Body  label="Bottom Plate"
  AllowCompound = false
  Group = -> [Binder001,Sketch,Pad,Sketch008,Pad006,Sketch014,Pad009,Chamfer]
  Origin = -> Origin
  Tip = -> Chamfer
FEATURE [Sketcher::SketchObject] Sketch015
  ArcFitTolerance = 1e-06
  AttachmentSupport = -> [XZ_Plane005]
  FullyConstrained = true
  MakeInternals = false
  MapMode = 5
  Placement = pos=(0,0,0) rot=(1,0,0;1.5708rad)
  expr: Constraints[17] = (dd.ButtonDiameter - 0.5) / 2
  expr: Constraints[18] = dd.ButtonDiameter / 2 + 1
  sketch-geometry (8):
    g0: LineSegment StartX=-5.25 StartY=15 StartZ=0 EndX=-5.25 EndY=10.5 EndZ=0
    g1: LineSegment StartX=-5.25 StartY=10.5 StartZ=0 EndX=-6.5 EndY=10.5 EndZ=0
    g2: LineSegment StartX=-6.5 StartY=10.5 StartZ=0 EndX=-6.5 EndY=9.5 EndZ=0
    g3: LineSegment StartX=-6.5 StartY=9.5 StartZ=0 EndX=-2 EndY=9.5 EndZ=0
    g4: LineSegment StartX=-2 StartY=9.5 StartZ=0 EndX=-2 EndY=0 EndZ=0
    g5: LineSegment StartX=-2 StartY=0 StartZ=0 EndX=0 EndY=0 EndZ=0
    g6: LineSegment StartX=0 StartY=0 StartZ=0 EndX=0 EndY=15 EndZ=0
    g7: LineSegment StartX=0 StartY=15 StartZ=0 EndX=-5.25 EndY=15 EndZ=0
  constraints (23):
    c: Vertical(g0)
    c: Coincident(g0,g1)
    c: Coincident(g1,g2)
    c: Coincident(g2,g3)
    c: Horizontal(g3)
    c: Coincident(g3,g4)
    c: Vertical(g4)
    c: Coincident(g4,g5)
    c: Coincident(g5,g6)
    c: Vertical(g6)
    c: Coincident(g6,g7)
    c: Coincident(g7,g0)
    c: Horizontal(g7)
    c: Horizontal(g1)
    c: Horizontal(g5)
    c: Vertical(g2)
    c: DistanceX(g5,g5) = 2
    c: DistanceX(g7,g7) = 5.25
    c: DistanceX(g1,g5) = 6.5
    c: DistanceY(g2,g2) = 1
    c: DistanceY(g0,g0) = 4.5
    c: DistanceY(g6,g6) = 15
    c: Coincident(g5,g-1)
FEATURE [PartDesign::Revolution] Revolution
  Angle = 360
  Angle2 = 60
  Axis = (0,2e-16,1)
  Base = (0,0,0)
  Placement = pos=(0,0,0) rot=(1,0,0;1.5708rad)
  Profile = -> Sketch015
  ReferenceAxis = -> Sketch015 [V_Axis]
  Refine = true
  Suppressed = false
  Type = 0
FEATURE [Sketcher::SketchObject] Sketch016
  ArcFitTolerance = 1e-06
  AttachmentOffset = pos=(0,0,14.01) rot=(0,0,1;0rad)
  AttachmentSupport = -> [XY_Plane006]
  FullyConstrained = true
  MakeInternals = false
  MapMode = 5
  Placement = pos=(0,0,14.01) rot=(0,0,1;0rad)
  sketch-geometry (9):
    g0: ArcOfCircle CenterX=0 CenterY=0 CenterZ=0 NormalX=0 NormalY=0 NormalZ=1 AngleXU=0 Radius=4 StartAngle=2.24593 EndAngle=7.17885
    g1: ArcOfCircle CenterX=2.25 CenterY=2.81025 CenterZ=0 NormalX=0 NormalY=0 NormalZ=1 AngleXU=0 Radius=0.4 StartAngle=0.895665 EndAngle=4.03726
    g2: ArcOfCircle CenterX=-2.25 CenterY=2.81025 CenterZ=0 NormalX=0 NormalY=0 NormalZ=1 AngleXU=0 Radius=0.4 StartAngle=5.38752 EndAngle=8.52911
    g3: ArcOfCircle CenterX=0 CenterY=0 CenterZ=0 NormalX=0 NormalY=0 NormalZ=1 AngleXU=0 Radius=3.2 StartAngle=2.24593 EndAngle=7.17885
    g4: ArcOfCircle CenterX=-4e-16 CenterY=1.56025 CenterZ=0 NormalX=0 NormalY=0 NormalZ=1 AngleXU=0 Radius=0.4 StartAngle=3.14159 EndAngle=6.28319
    g5: ArcOfCircle CenterX=-4e-16 CenterY=4.06025 CenterZ=0 NormalX=0 NormalY=0 NormalZ=1 AngleXU=0 Radius=0.4 StartAngle=2e-16 EndAngle=3.14159
    g6: LineSegment StartX=-0.4 StartY=1.56025 StartZ=0 EndX=-0.4 EndY=4.06025 EndZ=0
    g7: LineSegment StartX=0.4 StartY=1.56025 StartZ=0 EndX=0.4 EndY=4.06025 EndZ=0
    g8: GeomPoint [constr] X=-4e-16 Y=2.81025 Z=0
  constraints (20):
    c: Coincident(g0,g3)
    c: Tangent(g3,g2) = 1.5708
    c: Tangent(g3,g1) = 1.5708
    c: Tangent(g0,g2) = -1.5708
    c: Tangent(g0,g1) = -1.5708
    c: Radius(g2) = 0.4
    c: Coincident(g0,g-1)
    c: Horizontal(g2,g1)
    c: Diameter(g0) = 8
    c: DistanceX(g2,g1) = 4
    c: Tangent(g4,g6) = 1.5708
    c: Tangent(g4,g7) = -1.5708
    c: Tangent(g5,g6) = 1.5708
    c: Tangent(g5,g7) = -1.5708
    c: Equal(g4,g5)
    c: Vertical(g7)
    c: Distance(g4,g5) = 2.5
    c: Symmetric(g4,g5,g8)
    c: Symmetric(g1,g2,g8)
    c: Equal(g5,g2)
FEATURE [PartDesign::Pad] Pad010
  Direction = (0,0,1)
  Length = 1
  Length2 = 10
  Profile = -> Sketch016
  ReferenceAxis = -> Sketch016 [N_Axis]
  Refine = true
  Suppressed = false
  Type = 0
FEATURE [PartDesign::Body] Body006  label="Power symbol"
  AllowCompound = true
  Group = -> [Sketch016,Pad010]
  Origin = -> Origin006
  Tip = -> Pad010
FEATURE [PartDesign::Chamfer] Chamfer002
  Angle = 45
  Base = -> Revolution [Face7]
  BaseFeature = -> Revolution
  ChamferType = 0
  FlipDirection = false
  Placement = pos=(0,0,0) rot=(1,0,0;1.5708rad)
  Refine = true
  Size = 0.4
  Size2 = 1
  SupportTransform = false
  Suppressed = false
  UseAllEdges = false
FEATURE [PartDesign::Body] Body005  label="bare button"
  AllowCompound = false
  Group = -> [Sketch015,Revolution,Chamfer002]
  Origin = -> Origin005
  Tip = -> Chamfer002
FEATURE [Part::Compound] Compound  label="Power Button Extension"
  Links = -> [Body005,Body006]
FEATURE [PartDesign::SubShapeBinder] Binder003
  BindCopyOnChange = 0
  BindMode = 0
  ClaimChildren = false
  Context = -> Body007 [Binder003.]
  Fuse = false
  MakeFace = true
  OffsetFill = false
  OffsetIntersection = false
  OffsetJoinType = 0
  OffsetOpenResult = false
  PartialLoad = false
  Refine = true
  Relative = true
  Support = -> [Sketch005]
  _Version = 2
FEATURE [Sketcher::SketchObject] Sketch017
  ArcFitTolerance = 1e-06
  AttachmentSupport = -> [XY_Plane007]
  ExternalGeometry = -> [Binder003]
  FullyConstrained = true
  MakeInternals = false
  MapMode = 5
  sketch-geometry (11):
    g0: LineSegment StartX=-59.9 StartY=38.1 StartZ=0 EndX=-59.9 EndY=-38.1 EndZ=0
    g1: LineSegment StartX=-38.1 StartY=-59.9 StartZ=0 EndX=38.1 EndY=-59.9 EndZ=0
    g2: LineSegment StartX=59.9 StartY=-38.1 StartZ=0 EndX=59.9 EndY=38.1 EndZ=0
    g3: LineSegment StartX=38.1 StartY=59.9 StartZ=0 EndX=-38.1 EndY=59.9 EndZ=0
    g4: ArcOfCircle CenterX=-38.1 CenterY=38.1 CenterZ=0 NormalX=0 NormalY=0 NormalZ=1 AngleXU=0 Radius=21.8 StartAngle=1.5708 EndAngle=3.14159
    g5: ArcOfCircle CenterX=-38.1 CenterY=-38.1 CenterZ=0 NormalX=0 NormalY=0 NormalZ=1 AngleXU=0 Radius=21.8 StartAngle=3.14159 EndAngle=4.71239
    g6: ArcOfCircle CenterX=38.1 CenterY=-38.1 CenterZ=0 NormalX=0 NormalY=0 NormalZ=1 AngleXU=0 Radius=21.8 StartAngle=4.71239 EndAngle=6.28319
    g7: ArcOfCircle CenterX=38.1 CenterY=38.1 CenterZ=0 NormalX=0 NormalY=0 NormalZ=1 AngleXU=0 Radius=21.8 StartAngle=3e-16 EndAngle=1.5708
    g8: GeomPoint [constr] X=-59.9 Y=59.9 Z=0
    g9: GeomPoint [constr] X=59.9 Y=-59.9 Z=0
    g10: Circle CenterX=47.3762 CenterY=47.3762 CenterZ=0 NormalX=0 NormalY=0 NormalZ=1 AngleXU=0 Radius=5.5
  constraints (24):
    c: Tangent(g0,g4) = -1.5708
    c: Tangent(g0,g5) = -1.5708
    c: Tangent(g1,g5) = -1.5708
    c: Tangent(g1,g6) = -1.5708
    c: Tangent(g2,g6) = -1.5708
    c: Tangent(g2,g7) = -1.5708
    c: Tangent(g3,g7) = -1.5708
    c: Tangent(g3,g4) = -1.5708
    c: Vertical(g0)
    c: Vertical(g2)
    c: Horizontal(g1)
    c: Horizontal(g3)
    c: Equal(g4,g5)
    c: Equal(g5,g6)
    c: Equal(g6,g7)
    c: PointOnObject(g8,g0)
    c: PointOnObject(g8,g3)
    c: PointOnObject(g9,g1)
    c: PointOnObject(g9,g2)
    c: Coincident(g10,g-4)
    c: Equal(g10,g-4)
    c: Symmetric(g7,g5,g-1)
    c: Equal(g3,g0)
    c: Coincident(g3,g-3)
FEATURE [PartDesign::Body] Body007  label="Filter Cut Pattern"
  AllowCompound = false
  Group = -> [Binder003,Sketch017]
  Origin = -> Origin007
FEATURE [Sketcher::SketchObject] Sketch018  label="Apple Logo001"
  ArcFitTolerance = 1e-06
  AttachmentOffset = pos=(-107,158,0) rot=(0,0,1;0rad)
  AttachmentSupport = -> [Fusion]
  FullyConstrained = false
  MakeInternals = false
  MapMode = 5
  Placement = pos=(-107,158,1.6) rot=(0,0,1;0rad)
  sketch-geometry (19):
    g0: BSplineCurve PolesCount=4 KnotsCount=2 Degree=3 IsPeriodic=0
    g1: BSplineCurve PolesCount=4 KnotsCount=2 Degree=3 IsPeriodic=0
    g2: BSplineCurve PolesCount=4 KnotsCount=2 Degree=3 IsPeriodic=0
    g3: BSplineCurve PolesCount=4 KnotsCount=2 Degree=3 IsPeriodic=0
    g4: BSplineCurve PolesCount=4 KnotsCount=2 Degree=3 IsPeriodic=0
    g5: BSplineCurve PolesCount=4 KnotsCount=2 Degree=3 IsPeriodic=0
    g6: BSplineCurve PolesCount=4 KnotsCount=2 Degree=3 IsPeriodic=0
    g7: BSplineCurve PolesCount=4 KnotsCount=2 Degree=3 IsPeriodic=0
    g8: BSplineCurve PolesCount=4 KnotsCount=2 Degree=3 IsPeriodic=0
    g9: BSplineCurve PolesCount=4 KnotsCount=2 Degree=3 IsPeriodic=0
    g10: BSplineCurve PolesCount=4 KnotsCount=2 Degree=3 IsPeriodic=0
    g11: BSplineCurve PolesCount=4 KnotsCount=2 Degree=3 IsPeriodic=0
    g12: BSplineCurve PolesCount=4 KnotsCount=2 Degree=3 IsPeriodic=0
    g13: BSplineCurve PolesCount=4 KnotsCount=2 Degree=3 IsPeriodic=0
    g14: BSplineCurve PolesCount=4 KnotsCount=2 Degree=3 IsPeriodic=0
    g15: BSplineCurve PolesCount=4 KnotsCount=2 Degree=3 IsPeriodic=0
    g16: BSplineCurve PolesCount=4 KnotsCount=2 Degree=3 IsPeriodic=0
    g17: BSplineCurve PolesCount=4 KnotsCount=2 Degree=3 IsPeriodic=0
    g18: BSplineCurve PolesCount=4 KnotsCount=2 Degree=3 IsPeriodic=0
  constraints (19):
    c: Coincident(g0,g1)
    c: Coincident(g1,g2)
    c: Coincident(g2,g3)
    c: Coincident(g3,g4)
    c: Coincident(g4,g5)
    c: Coincident(g5,g6)
    c: Coincident(g6,g7)
    c: Coincident(g7,g8)
    c: Coincident(g8,g9)
    c: Coincident(g9,g10)
    c: Coincident(g10,g11)
    c: Coincident(g11,g0)
    c: Coincident(g12,g13)
    c: Coincident(g13,g14)
    c: Coincident(g14,g15)
    c: Coincident(g15,g16)
    c: Coincident(g16,g17)
    c: Coincident(g17,g18)
    c: Coincident(g18,g12)
FEATURE [Part::Extrusion] Extrude002  label="Apple Logo002"
  Base = -> Sketch018
  Dir = (0,0,1)
  DirMode = 2
  FaceMakerClass = Part::FaceMakerBullseye
  FaceMakerMode = 3
  LengthFwd = 0.4
  LengthRev = 0
  Reversed = true
  Solid = true
  Symmetric = false
FEATURE [Part::Compound] Compound001  label="Top Assembly"
  Links = -> [Extrude002,Fusion]
